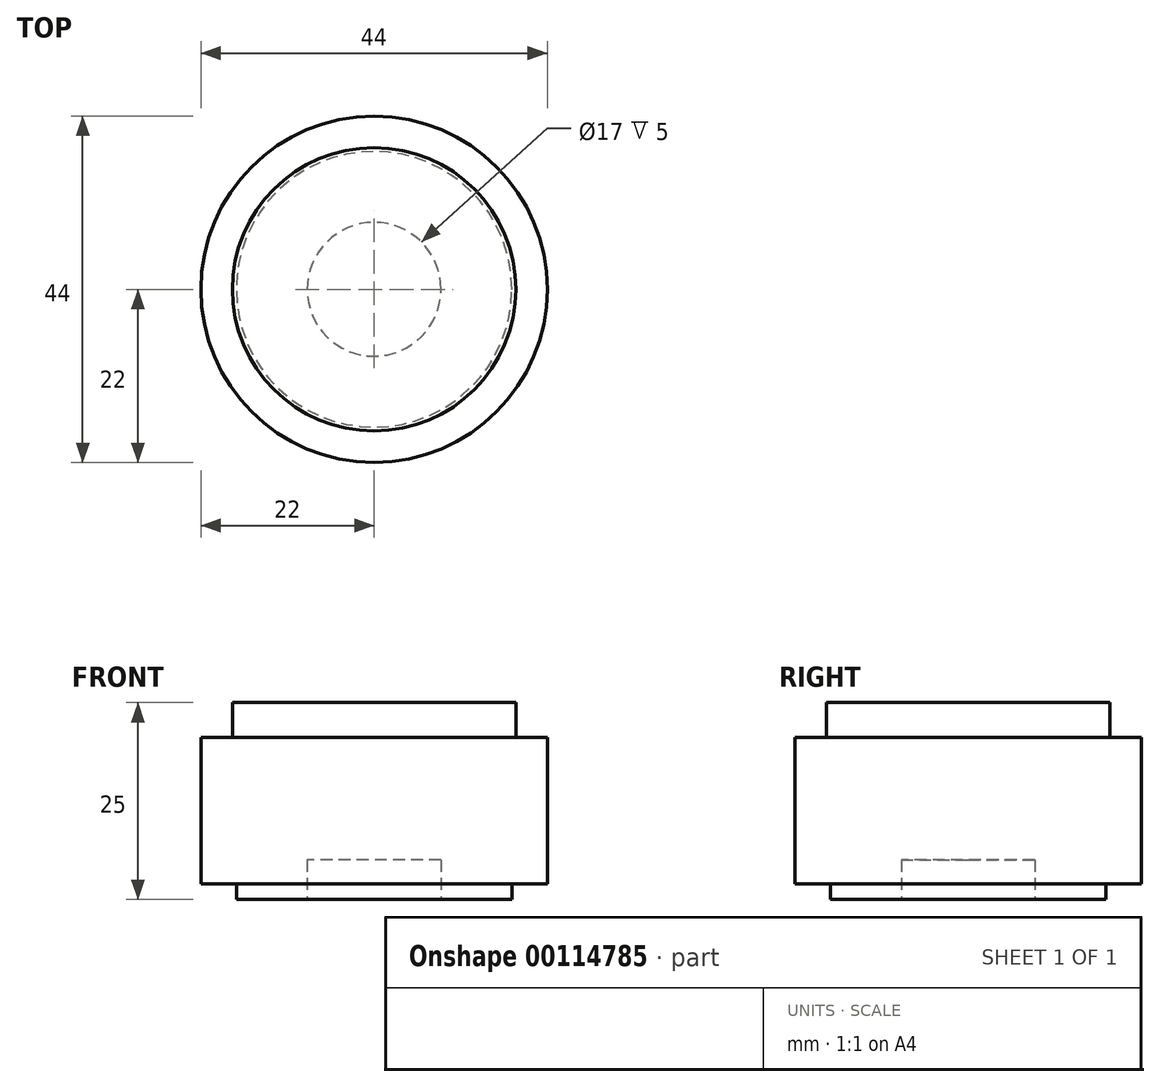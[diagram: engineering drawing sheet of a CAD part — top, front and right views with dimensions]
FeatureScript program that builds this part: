
annotation { "Feature Type Name" : "Feature", "Feature Type Description" : "" }
export const myFeature = defineFeature(function(context is Context, id is Id, definition is map)
    precondition{}
    {
        {
            var Q0;
            Q0=qCreatedBy(makeId("Top.planeOp"),FACE);
            var sketch = newSketch(context, id + "F0", { "sketchPlane" : qUnion([Q0])});
            skCircle(sketch, "E0", {"center": v(0, 0) * mm, "radius": 22 * mm});
            skCircle(sketch, "E1", {"center": v(0, 0) * mm, "radius": 8.5 * mm});
            skCircle(sketch, "E2", {"center": v(0, 0) * mm, "radius": 17.5 * mm});
            skSolve(sketch);
        }
        {
            var Q0;
            Q0=makeQuery(id+"F0.imprint","IMPRINT",FACE,{"disambiguationData":[TD([[makeQuery(id+"F0.imprint","IMPRINT",EDGE,{"derivedFrom":sQuery(id+"F0.wireOp",EDGE,"E0")}),1.0]])]});
            var Q1;
            Q1=makeQuery(id+"F0.imprint","IMPRINT",FACE,{"disambiguationData":[TD([[makeQuery(id+"F0.imprint","IMPRINT",EDGE,{"derivedFrom":sQuery(id+"F0.wireOp",EDGE,"E1")}),-1.0]])]});
            var Q2;
            Q2=makeQuery(id+"F0.imprint","IMPRINT",FACE,{"disambiguationData":[TD([[makeQuery(id+"F0.imprint","IMPRINT",EDGE,{"derivedFrom":sQuery(id+"F0.wireOp",EDGE,"E1")}),1.0]])]});
            extrude(context, id + "F1", {"entities" : qUnion([Q0, Q1, Q2]), "depth" : 25 * mm});
        }
        {
            var Q0;
            Q0=makeQuery(id+"F0.imprint","IMPRINT",FACE,{"disambiguationData":[TD([[makeQuery(id+"F0.imprint","IMPRINT",EDGE,{"derivedFrom":sQuery(id+"F0.wireOp",EDGE,"E1")}),1.0]])]});
            extrude(context, id + "F2", {"entities" : qUnion([Q0]), "operationType" : NewBodyOperationType.REMOVE, "depth" : 5 * mm});
        }
        {
            var Q0;
            Q0=makeQuery(id+"F0.imprint","IMPRINT",FACE,{"disambiguationData":[TD([[makeQuery(id+"F0.imprint","IMPRINT",EDGE,{"derivedFrom":sQuery(id+"F0.wireOp",EDGE,"E0")}),1.0]])]});
            extrude(context, id + "F3", {"entities" : qUnion([Q0]), "operationType" : NewBodyOperationType.REMOVE, "depth" : 2 * mm});
        }
        {
            var Q0;
            Q0=makeQuery(id+"F1.opExtrude","CAP_FACE",FACE,{"disambiguationData":[OSD([sQuery(id+"F0.wireOp",EDGE,"E0")])],"isStart":false});
            var sketch = newSketch(context, id + "F4", { "sketchPlane" : qUnion([Q0])});
            skCircle(sketch, "E3", {"center": v(0, 0) * mm, "radius": 18 * mm});
            skSolve(sketch);
        }
        {
            var Q0;
            Q0=makeQuery(id+"F4.imprint","IMPRINT",FACE,{"disambiguationData":[TD([[makeQuery(id+"F4.imprint","IMPRINT",EDGE,{"derivedFrom":sQuery(id+"F4.wireOp",EDGE,"E3")}),-1.0]])]});
            extrude(context, id + "F5", {"entities" : qUnion([Q0]), "operationType" : NewBodyOperationType.REMOVE, "oppositeDirection" : true, "depth" : 4.4 * mm});
        }
    });
